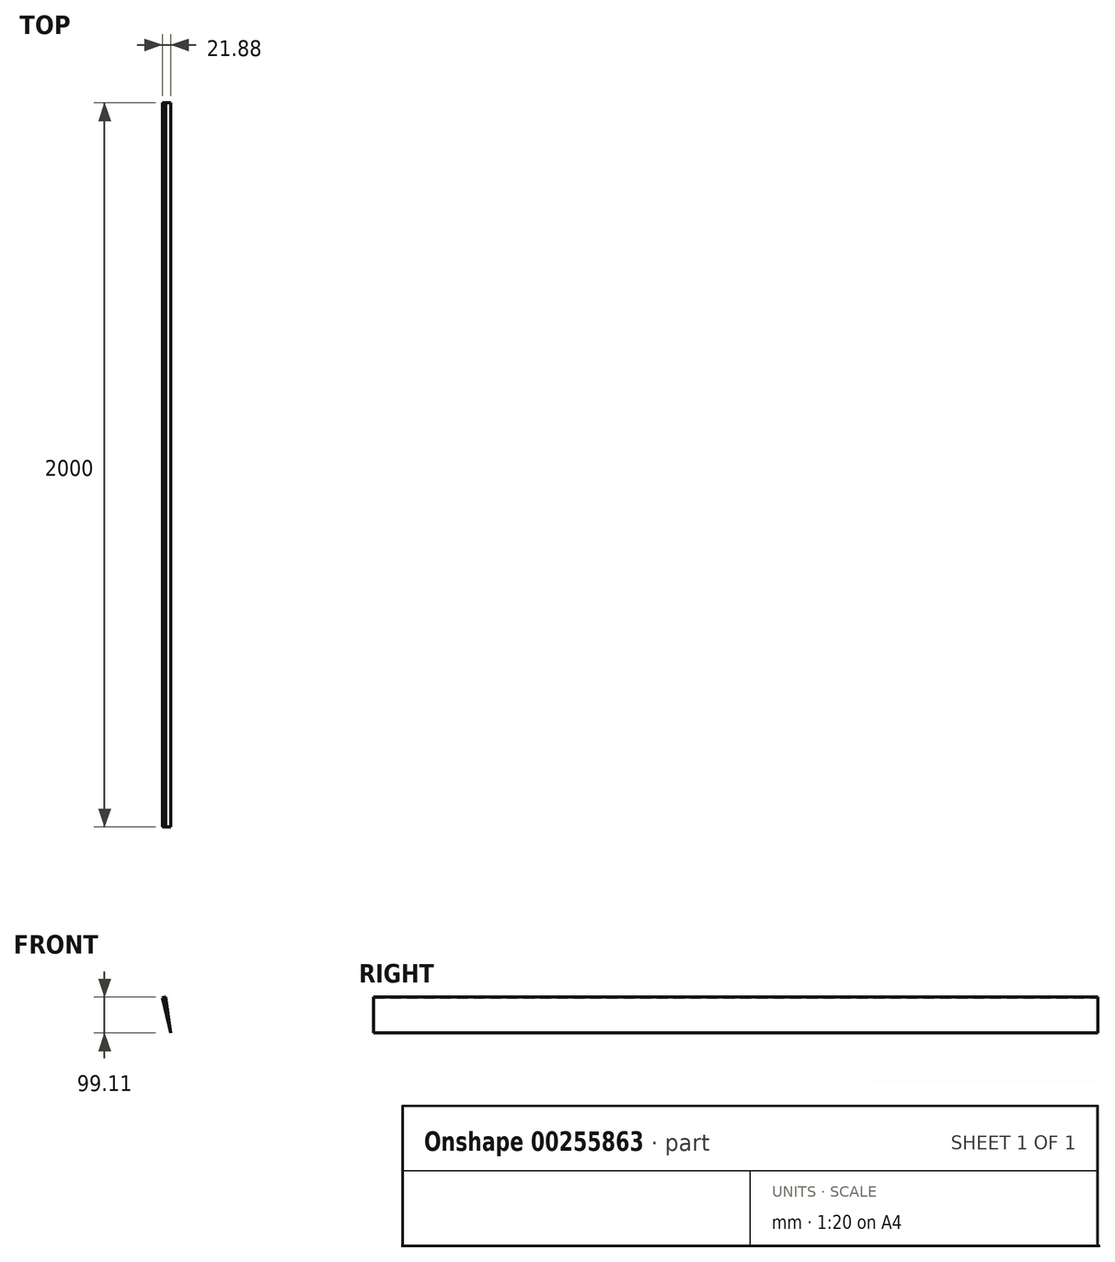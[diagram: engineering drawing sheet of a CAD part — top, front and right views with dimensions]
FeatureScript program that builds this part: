
annotation { "Feature Type Name" : "Feature", "Feature Type Description" : "" }
export const myFeature = defineFeature(function(context is Context, id is Id, definition is map)
    precondition{}
    {
        {
            var Q0;
            Q0=qCreatedBy(makeId("Front.planeOp"),FACE);
            var sketch = newSketch(context, id + "F0", { "sketchPlane" : qUnion([Q0])});
            skCircle(sketch, "E0", {"center": v(0, 0) * mm, "radius": 100 * mm});
            skLineSegment(sketch, "E1", {"start": v(0, 0) * mm, "end": v(-21.88, 97.58) * mm});
            skLineSegment(sketch, "E2", {"start": v(0, 0) * mm, "end": v(-13.3, 99.11) * mm});
            skSolve(sketch);
        }
        {
            var Q0;
            {var subQ0=sQuery(id+"F0.wireOp",EDGE,"E1");Q0=makeQuery(id+"F0.imprint","IMPRINT",FACE,{"disambiguationData":[TD([[makeQuery(id+"F0.imprint","IMPRINT",EDGE,{"derivedFrom":subQ0}),-1.0]])]});}
            extrude(context, id + "F1", {"entities" : qUnion([Q0]), "depth" : 2000 * mm, "offsetDistance" : 25 * mm});
        }
    });
